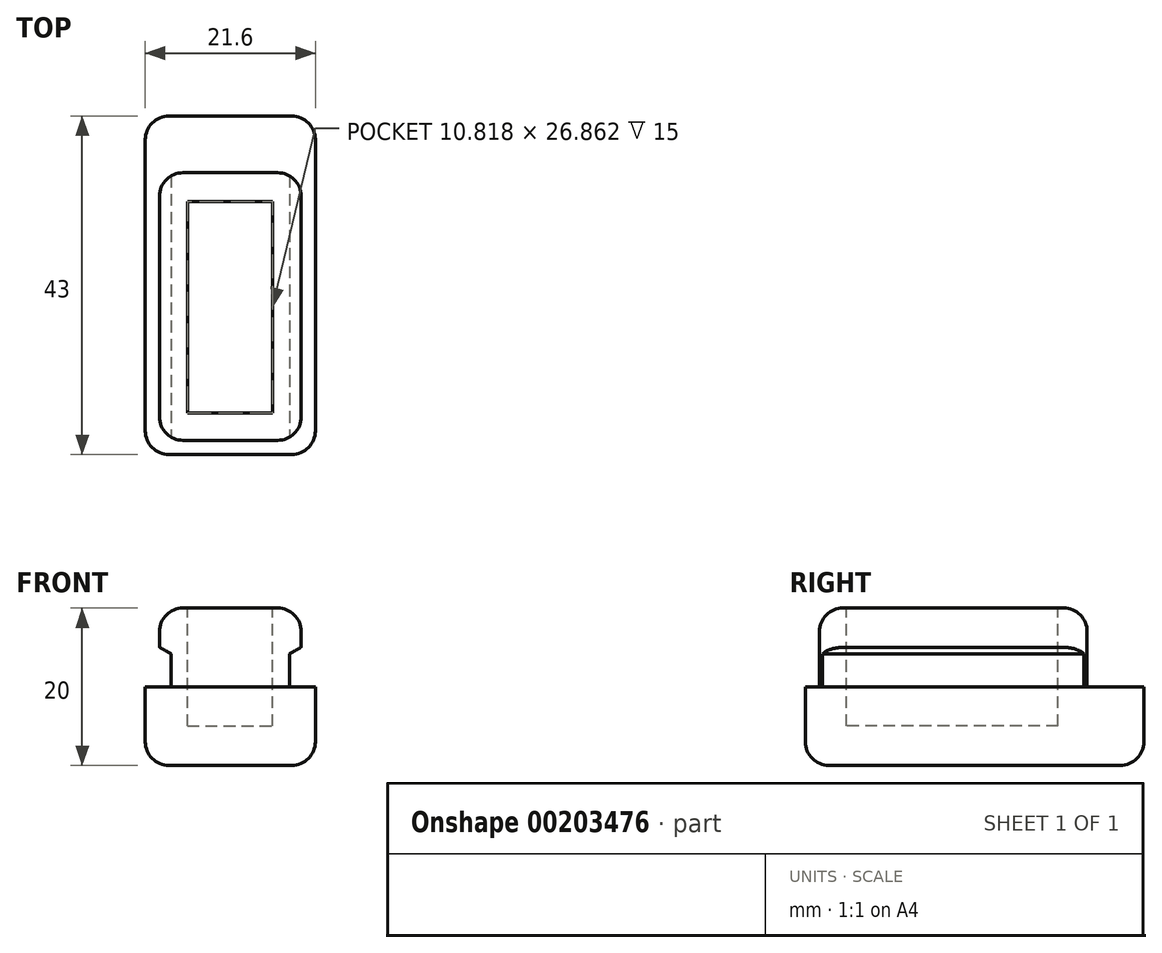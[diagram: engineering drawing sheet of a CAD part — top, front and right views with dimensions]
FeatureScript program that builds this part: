
annotation { "Feature Type Name" : "Feature", "Feature Type Description" : "" }
export const myFeature = defineFeature(function(context is Context, id is Id, definition is map)
    precondition{}
    {
        {
            var Q0;
            Q0=qCreatedBy(makeId("Top.planeOp"),FACE);
            var sketch = newSketch(context, id + "F0", { "sketchPlane" : qUnion([Q0])});
            skLineSegment(sketch, "E0.bottom", {"start": v(0, 0) * mm, "end": v(21.6, 0) * mm});
            skLineSegment(sketch, "E0.top", {"start": v(0, 43) * mm, "end": v(21.6, 43) * mm});
            skLineSegment(sketch, "E0.left", {"start": v(0, 0) * mm, "end": v(0, 43) * mm});
            skLineSegment(sketch, "E0.right", {"start": v(21.6, 0) * mm, "end": v(21.6, 43) * mm});
            skSolve(sketch);
        }
        {
            var Q0;
            Q0=makeQuery(id+"F0.imprint","IMPRINT",FACE,{"disambiguationData":[TD([[makeQuery(id+"F0.imprint","IMPRINT",EDGE,{"derivedFrom":sQuery(id+"F0.wireOp",EDGE,"E0.bottom")}),1.0]])]});
            extrude(context, id + "F1", {"entities" : qUnion([Q0]), "depth" : 10 * mm});
        }
        {
            var Q0;
            Q0=makeQuery(id+"F1.opExtrude","CAP_FACE",FACE,{"disambiguationData":[OSD([sQuery(id+"F0.wireOp",EDGE,"E0.bottom"),sQuery(id+"F0.wireOp",EDGE,"E0.top"),sQuery(id+"F0.wireOp",EDGE,"E0.left"),sQuery(id+"F0.wireOp",EDGE,"E0.right")])],"isStart":false});
            var sketch = newSketch(context, id + "F2", { "sketchPlane" : qUnion([Q0])});
            skLineSegment(sketch, "E1.bottom", {"start": v(1.8, 1.8) * mm, "end": v(19.8, 1.8) * mm});
            skLineSegment(sketch, "E1.top", {"start": v(1.8, 35.8) * mm, "end": v(19.8, 35.8) * mm});
            skLineSegment(sketch, "E1.left", {"start": v(1.8, 1.8) * mm, "end": v(1.8, 35.8) * mm});
            skLineSegment(sketch, "E1.right", {"start": v(19.8, 1.8) * mm, "end": v(19.8, 35.8) * mm});
            skSolve(sketch);
        }
        {
            var Q0;
            Q0 = qSketchRegion(id + "F2", true);
            extrude(context, id + "F3", {"entities" : qUnion([Q0]), "operationType" : NewBodyOperationType.ADD, "depth" : 10 * mm});
        }
        {
            var Q0;
            Q0=makeQuery(id+"F3.opExtrude","CAP_FACE",FACE,{"disambiguationData":[OSD([sQuery(id+"F2.wireOp",EDGE,"E1.bottom"),sQuery(id+"F2.wireOp",EDGE,"E1.top"),sQuery(id+"F2.wireOp",EDGE,"E1.left"),sQuery(id+"F2.wireOp",EDGE,"E1.right")])],"isStart":false});
            fillet(context, id + "F4", {"entities" : qUnion([Q0]), "radius" : 3 * mm, "tangentPropagation" : true, "allowEdgeOverflow" : false});
        }
        {
            var Q0;
            Q0=makeQuery(id+"F3.opExtrude","SWEPT_EDGE",EDGE,{"disambiguationData":[OSD([sQuery(id+"F2.wireOp",EDGE,"E1.bottom"),sQuery(id+"F2.wireOp",EDGE,"E1.right")])]});
            var Q1;
            Q1=makeQuery(id+"F3.opExtrude","SWEPT_EDGE",EDGE,{"disambiguationData":[OSD([sQuery(id+"F2.wireOp",EDGE,"E1.top"),sQuery(id+"F2.wireOp",EDGE,"E1.right")])]});
            var Q2;
            Q2=makeQuery(id+"F3.opExtrude","SWEPT_EDGE",EDGE,{"disambiguationData":[OSD([sQuery(id+"F2.wireOp",EDGE,"E1.top"),sQuery(id+"F2.wireOp",EDGE,"E1.left")])]});
            var Q3;
            Q3=makeQuery(id+"F3.opExtrude","SWEPT_EDGE",EDGE,{"disambiguationData":[OSD([sQuery(id+"F2.wireOp",EDGE,"E1.bottom"),sQuery(id+"F2.wireOp",EDGE,"E1.left")])]});
            fillet(context, id + "F5", {"entities" : qUnion([Q0, Q1, Q2, Q3]), "radius" : 3 * mm, "tangentPropagation" : true, "allowEdgeOverflow" : false});
        }
        {
            var Q0;
            Q0=makeQuery(id+"F1.opExtrude","SWEPT_EDGE",EDGE,{"disambiguationData":[OSD([sQuery(id+"F0.wireOp",EDGE,"E0.bottom"),sQuery(id+"F0.wireOp",EDGE,"E0.right")])]});
            var Q1;
            Q1=makeQuery(id+"F1.opExtrude","SWEPT_EDGE",EDGE,{"disambiguationData":[OSD([sQuery(id+"F0.wireOp",EDGE,"E0.bottom"),sQuery(id+"F0.wireOp",EDGE,"E0.left")])]});
            var Q2;
            Q2=makeQuery(id+"F1.opExtrude","SWEPT_EDGE",EDGE,{"disambiguationData":[OSD([sQuery(id+"F0.wireOp",EDGE,"E0.top"),sQuery(id+"F0.wireOp",EDGE,"E0.left")])]});
            var Q3;
            Q3=makeQuery(id+"F1.opExtrude","SWEPT_EDGE",EDGE,{"disambiguationData":[OSD([sQuery(id+"F0.wireOp",EDGE,"E0.top"),sQuery(id+"F0.wireOp",EDGE,"E0.right")])]});
            var Q4;
            Q4=makeQuery(id+"F1.opExtrude","CAP_EDGE",EDGE,{"disambiguationData":[OSD([sQuery(id+"F0.wireOp",EDGE,"E0.bottom")])],"isStart":true});
            var Q5;
            Q5=makeQuery(id+"F1.opExtrude","CAP_EDGE",EDGE,{"disambiguationData":[OSD([sQuery(id+"F0.wireOp",EDGE,"E0.right")])],"isStart":true});
            var Q6;
            Q6=makeQuery(id+"F1.opExtrude","CAP_EDGE",EDGE,{"disambiguationData":[OSD([sQuery(id+"F0.wireOp",EDGE,"E0.left")])],"isStart":true});
            var Q7;
            Q7=makeQuery(id+"F1.opExtrude","CAP_EDGE",EDGE,{"disambiguationData":[OSD([sQuery(id+"F0.wireOp",EDGE,"E0.top")])],"isStart":true});
            fillet(context, id + "F6", {"entities" : qUnion([Q0, Q1, Q2, Q3, Q4, Q5, Q6, Q7]), "radius" : 3 * mm, "tangentPropagation" : true, "allowEdgeOverflow" : false});
        }
        {
            var Q0;
            Q0=makeQuery(id+"F3.opExtrude","CAP_FACE",FACE,{"disambiguationData":[OSD([sQuery(id+"F2.wireOp",EDGE,"E1.bottom"),sQuery(id+"F2.wireOp",EDGE,"E1.top"),sQuery(id+"F2.wireOp",EDGE,"E1.left"),sQuery(id+"F2.wireOp",EDGE,"E1.right")])],"isStart":false});
            var sketch = newSketch(context, id + "F7", { "sketchPlane" : qUnion([Q0])});
            skLineSegment(sketch, "E2.bottom", {"start": v(5.34, 32.1) * mm, "end": v(16.16, 32.1) * mm});
            skLineSegment(sketch, "E2.top", {"start": v(5.34, 5.25) * mm, "end": v(16.16, 5.25) * mm});
            skLineSegment(sketch, "E2.left", {"start": v(5.34, 32.1) * mm, "end": v(5.34, 5.25) * mm});
            skLineSegment(sketch, "E2.right", {"start": v(16.16, 32.1) * mm, "end": v(16.16, 5.25) * mm});
            skSolve(sketch);
        }
        {
            var Q0;
            Q0 = qSketchRegion(id + "F7", true);
            extrude(context, id + "F8", {"entities" : qUnion([Q0]), "operationType" : NewBodyOperationType.REMOVE, "oppositeDirection" : true, "depth" : 15 * mm});
        }
        {
            var Q0;
            Q0=makeQuery(id+"F3.opExtrude","SWEPT_FACE",FACE,{"disambiguationData":[OSD([sQuery(id+"F2.wireOp",EDGE,"E1.right")])]});
            var sketch = newSketch(context, id + "F9", { "sketchPlane" : qUnion([Q0])});
            skLineSegment(sketch, "E3.bottom", {"start": v(42.68, 10) * mm, "end": v(-17.18, 10) * mm});
            skLineSegment(sketch, "E3.top", {"start": v(42.68, 15) * mm, "end": v(-17.18, 15) * mm});
            skLineSegment(sketch, "E3.left", {"start": v(42.68, 10) * mm, "end": v(42.68, 15) * mm});
            skLineSegment(sketch, "E3.right", {"start": v(-17.18, 10) * mm, "end": v(-17.18, 15) * mm});
            skSolve(sketch);
        }
        {
            var Q0;
            Q0 = qSketchRegion(id + "F9", true);
            extrude(context, id + "F10", {"entities" : qUnion([Q0]), "operationType" : NewBodyOperationType.REMOVE, "oppositeDirection" : true, "depth" : 1.5 * mm});
        }
        {
            var Q0;
            Q0=makeQuery(id+"F10.boolean.opBoolean","COPY",EDGE,{"derivedFrom":makeQuery(id+"F10.opExtrude","CAP_EDGE",EDGE,{"disambiguationData":[OSD([sQuery(id+"F9.wireOp",EDGE,"E3.top")])],"isStart":false})});
            chamfer(context, id + "F11", {"entities" : qUnion([Q0]), "chamferType" : ChamferType.TWO_OFFSETS, "width1" : 0.8 * mm, "oppositeDirection" : false, "width2" : 1.5 * mm, "tangentPropagation" : true});
        }
        {
            var Q0;
            Q0=makeQuery(id+"F3.opExtrude","SWEPT_FACE",FACE,{"disambiguationData":[OSD([sQuery(id+"F2.wireOp",EDGE,"E1.left")])]});
            var sketch = newSketch(context, id + "F12", { "sketchPlane" : qUnion([Q0])});
            skLineSegment(sketch, "E4.bottom", {"start": v(-49.08, 10) * mm, "end": v(38.15, 10) * mm});
            skLineSegment(sketch, "E4.top", {"start": v(-49.08, 15) * mm, "end": v(38.15, 15) * mm});
            skLineSegment(sketch, "E4.left", {"start": v(-49.08, 10) * mm, "end": v(-49.08, 15) * mm});
            skLineSegment(sketch, "E4.right", {"start": v(38.15, 10) * mm, "end": v(38.15, 15) * mm});
            skSolve(sketch);
        }
        {
            var Q0;
            Q0 = qSketchRegion(id + "F12", true);
            extrude(context, id + "F13", {"entities" : qUnion([Q0]), "operationType" : NewBodyOperationType.REMOVE, "oppositeDirection" : true, "depth" : 1.5 * mm});
        }
        {
            var Q0;
            Q0=makeQuery(id+"F13.boolean.opBoolean","COPY",EDGE,{"derivedFrom":makeQuery(id+"F13.opExtrude","CAP_EDGE",EDGE,{"disambiguationData":[OSD([sQuery(id+"F12.wireOp",EDGE,"E4.top")])],"isStart":false})});
            chamfer(context, id + "F14", {"entities" : qUnion([Q0]), "chamferType" : ChamferType.TWO_OFFSETS, "width1" : 1.5 * mm, "oppositeDirection" : false, "width2" : 0.8 * mm, "tangentPropagation" : true});
        }
    });
